# Revit family: Gira_5569920
name_source: partatom
category: Elektroinstallationen
revit_build: Autodesk Revit 2017 (Build: 20160225_1515(x64)
units: mm (PartAtom-declared; Revit-internal decimal feet)

## family parameters
Basisbauteil = Fläche
Beim Laden mit Abzugskörper schneiden = Nein
Bemaßung runder Anschluss = Durchmesser verwenden
Beschriftungsausrichtung beibehalten = Nein
Gemeinsam genutzt = Nein
Raumberechnungspunkt = Nein
Teiletyp = Normal

## types (1)
- Gira_5569920
    BIM = https://media.stage.bim.site
    Beschreibung = Door st.mod.start-up btn S106 SST,System 106 door station module with start-up button,,stainless steel   start-up button,The Gira System 106 is an installation system made of metal in a puristic and elegant frameless design, based on basic measurements of 106.5 × 106.5 mm. With the modular door intercom in Gira System 106, hospitality begins even before you reach the front door. All the functions are presented in a harmonious overall appearance, from the call button module, intercom module, and camera module, up to the info and blank module. In the dark, backlit call buttons with inscription space ensure good legibility and an attractive appearance.,,Individually adaptable modular system, The System 106 can be used in family homes or apartment buildings, as well as in office buildings, industrial properties, and hotels. The modular design enables the system's size, design, and functionality to be individually adapted to the respective requirements. Expansions and changes are possible at any time by easily exchanging the modules.,With this system, it is also possible to exchange the fronts only. This means that the appearance of the system can be changed from e.g. traffic white to a stainless steel surface at a later stage, without having to exchange the electronic units.,,High-quality materials,The modules are frameless with design fronts made of genuine materials, available in two brushed stainless steel versions (V2A and V4A), anodised aluminium C-0, and a metal alloy lacquered in traffic white (RAL 9016): all robust materials which ensure durability. The camera and DIN 18040 display module feature a black glass cover.,,Easy and phased installation,The system can be installed in phases, in parallel to the progress of building work. In this way, it is possible to initially install only the lower part of a surface-mounted housing during construction of the shell; cables and modules can then be added when they are needed.,,Individual inscription options,Call button modules and info modules can be labelled individually via the Gira inscription service.,,Features:,- Compact intercom module with integrated call button for communication between indoors and outdoors.,- A high-quality microphone and weather-resistant speaker ensure clear communication.,- Power supply via 2-wire bus. Additional connector for AS (e.g. required for three or more camera modules).,- All other System 106 modules (except intercom module) are supplied with power via the door station module.,,Notes :,- Professional labelling with the Gira Inscription Service www.marking.gira.com.
    Data sheet = https://katalog.gira.de
    GTIN = 4010337022459
    HAN = 5569920
    Height [m] = 0.1065
    Hersteller = Gira
    Installation technique = Bus system
    Number of bell buttons = 1
    Productwebsite = http://katalog.gira.de
    Typname = Door st.mod. start-up btn System 106 stainl.steel
    URL = https://www.gira.de
    Vorgabe-Ansicht = 1219 mm
    Width [m] = 0.1065

## geometry (parser evidence)
native form markers: Sweep x2
no freeform markers — native parametric forms only
